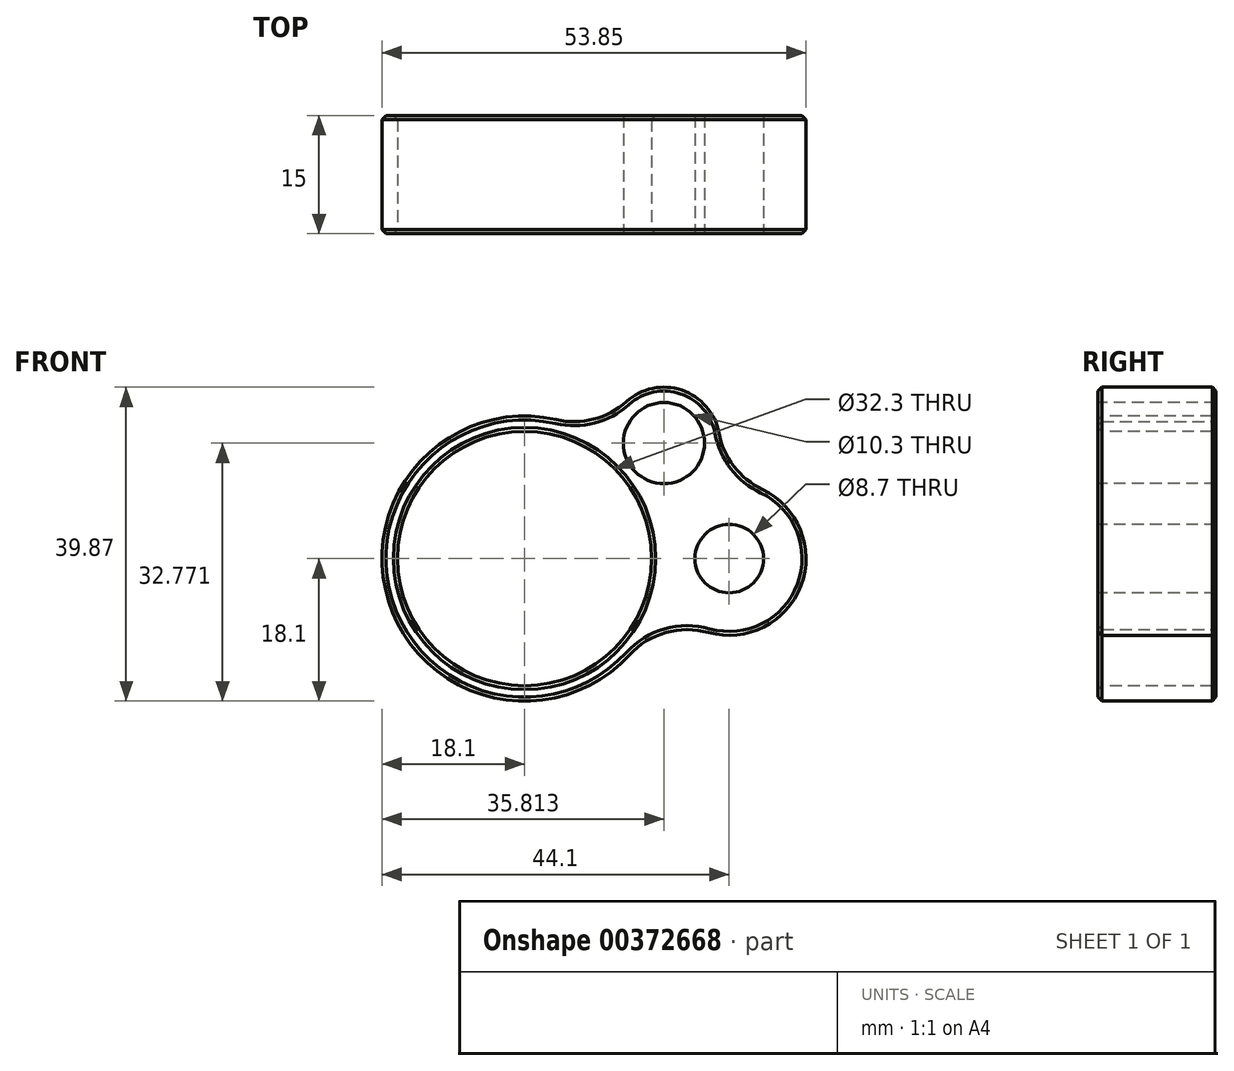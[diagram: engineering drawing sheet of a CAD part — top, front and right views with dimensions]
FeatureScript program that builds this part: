
annotation { "Feature Type Name" : "Feature", "Feature Type Description" : "" }
export const myFeature = defineFeature(function(context is Context, id is Id, definition is map)
    precondition{}
    {
        {
            var Q0;
            Q0=qCreatedBy(makeId("Front.planeOp"),FACE);
            var sketch = newSketch(context, id + "F0", { "sketchPlane" : qUnion([Q0])});
            skCircle(sketch, "E0", {"center": v(0, 0) * mm, "radius": 16.15 * mm});
            skArc(sketch, "E1", {"start": v(21.2, 8.49) * mm, "mid": v(21.29, 20.8) * mm, "end": v(10.61, 14.66) * mm});
            skArc(sketch, "E2", {"start": v(10.61, 14.66) * mm, "mid": v(-17.06, -6.04) * mm, "end": v(17.47, -4.73) * mm});
            skCircle(sketch, "E3.converted", {"center": v(17.71, 14.67) * mm, "radius": 5.15 * mm});
            skCircle(sketch, "E4", {"center": v(26, 0) * mm, "radius": 4.35 * mm});
            skArc(sketch, "E5", {"start": v(17.47, -4.73) * mm, "mid": v(35.38, -2.65) * mm, "end": v(21.2, 8.49) * mm});
            skLineSegment(sketch, "E6", {"start": v(0, 0) * mm, "end": v(19.71, 11.13) * mm, "construction": true});
            skLineSegment(sketch, "E7", {"start": v(17.71, 14.67) * mm, "end": v(26, 0) * mm, "construction": true});
            skSolve(sketch);
        }
        {
            var Q0;
            Q0=makeQuery(id+"F0.imprint","IMPRINT",FACE,{"disambiguationData":[TD([[makeQuery(id+"F0.imprint","IMPRINT",EDGE,{"derivedFrom":sQuery(id+"F0.wireOp",EDGE,"E0")}),-1.0]])]});
            var Q1;
            {var subQ0=sQuery(id+"F0.wireOp",EDGE,"E5");var subQ1=sQuery(id+"F0.wireOp",EDGE,"E1");var subQ2=makeQuery(id+"F0.imprint","INTERSECT",VERTEX,{"derivedFrom":[subQ1,subQ0]});Q1=makeQuery(id+"F0.imprint","IMPRINT",FACE,{"disambiguationData":[TD([[makeQuery(id+"F0.imprint","IMPRINT",EDGE,{"disambiguationData":[TD([[subQ2,-1.0]])],"derivedFrom":subQ1}),1.0]])]});}
            extrude(context, id + "F1", {"entities" : qUnion([Q0, Q1]), "oppositeDirection" : true, "depth" : 15 * mm, "offsetDistance" : 25 * mm});
        }
        {
            var Q0;
            Q0=makeQuery(id+"F1.opExtrude","SWEPT_EDGE",EDGE,{"disambiguationData":[OSD([sQuery(id+"F0.wireOp",EDGE,"E1"),sQuery(id+"F0.wireOp",EDGE,"E2")])]});
            var Q1;
            Q1=makeQuery(id+"F1.opExtrude","SWEPT_EDGE",EDGE,{"disambiguationData":[OSD([sQuery(id+"F0.wireOp",EDGE,"E1"),sQuery(id+"F0.wireOp",EDGE,"E5")])]});
            var Q2;
            Q2=makeQuery(id+"F1.opExtrude","SWEPT_EDGE",EDGE,{"disambiguationData":[OSD([sQuery(id+"F0.wireOp",EDGE,"E2"),sQuery(id+"F0.wireOp",EDGE,"E5")])]});
            fillet(context, id + "F2", {"entities" : qUnion([Q0, Q1, Q2]), "radius" : 10 * mm, "tangentPropagation" : true, "allowEdgeOverflow" : false});
        }
        {
            var Q0;
            Q0=makeQuery(id+"F1.opExtrude","CAP_EDGE",EDGE,{"disambiguationData":[OSD([sQuery(id+"F0.wireOp",EDGE,"E2")])],"isStart":true});
            var Q1;
            Q1=makeQuery(id+"F1.opExtrude","CAP_EDGE",EDGE,{"disambiguationData":[OSD([sQuery(id+"F0.wireOp",EDGE,"E2")])],"isStart":false});
            var Q2;
            Q2=makeQuery(id+"F1.opExtrude","CAP_EDGE",EDGE,{"disambiguationData":[OSD([sQuery(id+"F0.wireOp",EDGE,"E0")])],"isStart":false});
            var Q3;
            Q3=makeQuery(id+"F1.opExtrude","CAP_EDGE",EDGE,{"disambiguationData":[OSD([sQuery(id+"F0.wireOp",EDGE,"E0")])],"isStart":true});
            chamfer(context, id + "F3", {"entities" : qUnion([Q0, Q1, Q2, Q3]), "width" : 0.5 * mm, "tangentPropagation" : true});
        }
    });
